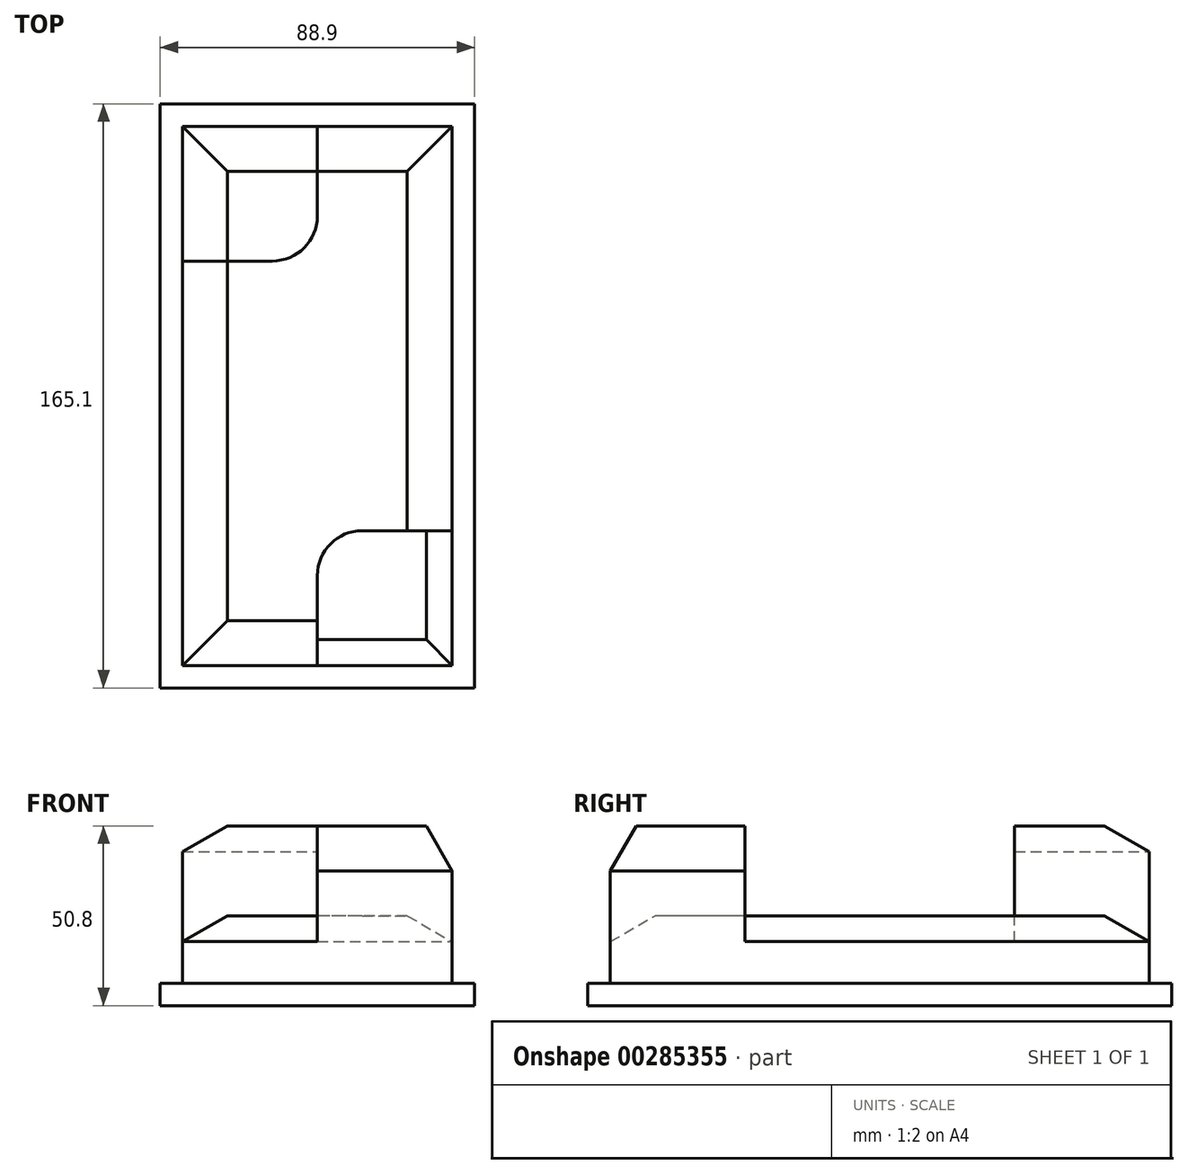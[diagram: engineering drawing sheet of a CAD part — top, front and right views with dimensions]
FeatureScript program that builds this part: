
annotation { "Feature Type Name" : "Feature", "Feature Type Description" : "" }
export const myFeature = defineFeature(function(context is Context, id is Id, definition is map)
    precondition{}
    {
        {
            var Q0;
            Q0=qCreatedBy(makeId("Top.planeOp"),FACE);
            var sketch = newSketch(context, id + "F0", { "sketchPlane" : qUnion([Q0])});
            skLineSegment(sketch, "E0.bottom", {"start": v(38.1, 76.2) * mm, "end": v(-38.1, 76.2) * mm});
            skLineSegment(sketch, "E0.top", {"start": v(38.1, -76.2) * mm, "end": v(-38.1, -76.2) * mm});
            skLineSegment(sketch, "E0.left", {"start": v(38.1, 76.2) * mm, "end": v(38.1, -76.2) * mm});
            skLineSegment(sketch, "E0.right", {"start": v(-38.1, 76.2) * mm, "end": v(-38.1, -76.2) * mm});
            skPoint(sketch, "E0.middle", {"position": v(0, 0) * mm});
            skLineSegment(sketch, "E1.bottom", {"start": v(44.45, -82.55) * mm, "end": v(-44.45, -82.55) * mm});
            skLineSegment(sketch, "E1.top", {"start": v(44.45, 82.55) * mm, "end": v(-44.45, 82.55) * mm});
            skLineSegment(sketch, "E1.left", {"start": v(44.45, -82.55) * mm, "end": v(44.45, 82.55) * mm});
            skLineSegment(sketch, "E1.right", {"start": v(-44.45, -82.55) * mm, "end": v(-44.45, 82.55) * mm});
            skLineSegment(sketch, "E2", {"start": v(0, 76.2) * mm, "end": v(0, 50.8) * mm});
            skLineSegment(sketch, "E3", {"start": v(-12.7, 38.1) * mm, "end": v(-38.1, 38.1) * mm});
            skLineSegment(sketch, "E4", {"start": v(12.7, -38.1) * mm, "end": v(38.1, -38.1) * mm});
            skLineSegment(sketch, "E5", {"start": v(0, -50.8) * mm, "end": v(0, -76.2) * mm});
            skPoint(sketch, "E6.visualSharp", {"position": v(0, 38.1) * mm});
            skArc(sketch, "E6.filletArc", {"start": v(-12.7, 38.1) * mm, "mid": v(-3.72, 41.82) * mm, "end": v(0, 50.8) * mm});
            skPoint(sketch, "E7.visualSharp", {"position": v(0, -38.1) * mm});
            skArc(sketch, "E7.filletArc", {"start": v(12.7, -38.1) * mm, "mid": v(3.72, -41.82) * mm, "end": v(0, -50.8) * mm});
            skSolve(sketch);
        }
        {
            var Q0;
            Q0=makeQuery(id+"F0.imprint","IMPRINT",FACE,{"disambiguationData":[TD([[makeQuery(id+"F0.imprint","IMPRINT",EDGE,{"derivedFrom":sQuery(id+"F0.wireOp",EDGE,"E1.bottom")}),-1.0]])]});
            extrude(context, id + "F1", {"entities" : qUnion([Q0]), "depth" : 6.35 * mm});
        }
        {
            var Q0;
            {var subQ9=sQuery(id+"F0.wireOp",EDGE,"E2");Q0=makeQuery(id+"F0.imprint","IMPRINT",FACE,{"disambiguationData":[TD([[makeQuery(id+"F0.imprint","IMPRINT",EDGE,{"derivedFrom":subQ9}),1.0]])]});}
            extrude(context, id + "F2", {"entities" : qUnion([Q0]), "operationType" : NewBodyOperationType.ADD, "depth" : 25.4 * mm});
        }
        {
            var Q0;
            {var subQ1=sQuery(id+"F0.wireOp",EDGE,"E2");Q0=makeQuery(id+"F0.imprint","IMPRINT",FACE,{"disambiguationData":[TD([[makeQuery(id+"F0.imprint","IMPRINT",EDGE,{"derivedFrom":subQ1}),-1.0]])]});}
            var Q1;
            {var subQ0=sQuery(id+"F0.wireOp",EDGE,"E4");Q1=makeQuery(id+"F0.imprint","IMPRINT",FACE,{"disambiguationData":[TD([[makeQuery(id+"F0.imprint","IMPRINT",EDGE,{"derivedFrom":subQ0}),-1.0]])]});}
            extrude(context, id + "F3", {"entities" : qUnion([Q0, Q1]), "operationType" : NewBodyOperationType.ADD, "depth" : 50.8 * mm});
        }
        {
            var Q0;
            Q0=makeQuery(id+"F2.opExtrude","CAP_EDGE",EDGE,{"disambiguationData":[OSD([sQuery(id+"F0.wireOp",EDGE,"E0.right")])],"isStart":false});
            var Q1;
            Q1=makeQuery(id+"F2.opExtrude","CAP_EDGE",EDGE,{"disambiguationData":[OSD([sQuery(id+"F0.wireOp",EDGE,"E0.bottom")])],"isStart":false});
            var Q2;
            Q2=makeQuery(id+"F2.opExtrude","CAP_EDGE",EDGE,{"disambiguationData":[OSD([sQuery(id+"F0.wireOp",EDGE,"E0.left")])],"isStart":false});
            var Q3;
            Q3=makeQuery(id+"F2.opExtrude","CAP_EDGE",EDGE,{"disambiguationData":[OSD([sQuery(id+"F0.wireOp",EDGE,"E0.top")])],"isStart":false});
            chamfer(context, id + "F4", {"entities" : qUnion([Q0, Q1, Q2, Q3]), "chamferType" : ChamferType.OFFSET_ANGLE, "width" : 12.7 * mm, "oppositeDirection" : false, "angle" : 30 * degree, "tangentPropagation" : true});
        }
        {
            var Q0;
            Q0=makeQuery(id+"F3.opExtrude","CAP_EDGE",EDGE,{"disambiguationData":[OSD([sQuery(id+"F0.wireOp",EDGE,"E0.left")])],"isStart":false});
            var Q1;
            Q1=makeQuery(id+"F3.opExtrude","CAP_EDGE",EDGE,{"disambiguationData":[OSD([sQuery(id+"F0.wireOp",EDGE,"E0.top")])],"isStart":false});
            var Q2;
            Q2=makeQuery(id+"F3.opExtrude","CAP_EDGE",EDGE,{"disambiguationData":[OSD([sQuery(id+"F0.wireOp",EDGE,"E0.bottom")])],"isStart":false});
            var Q3;
            Q3=makeQuery(id+"F3.opExtrude","CAP_EDGE",EDGE,{"disambiguationData":[OSD([sQuery(id+"F0.wireOp",EDGE,"E0.right")])],"isStart":false});
            chamfer(context, id + "F5", {"entities" : qUnion([Q0, Q1, Q2, Q3]), "chamferType" : ChamferType.OFFSET_ANGLE, "width" : 12.7 * mm, "oppositeDirection" : false, "angle" : 30 * degree, "tangentPropagation" : true});
        }
    });
